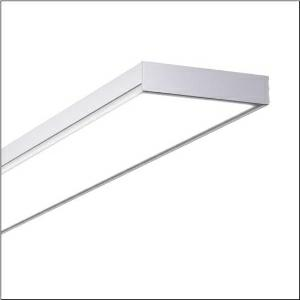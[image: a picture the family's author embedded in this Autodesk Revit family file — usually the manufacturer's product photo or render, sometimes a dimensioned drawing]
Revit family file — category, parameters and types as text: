
# Revit family: apollon_r__31_51mp25wm2441e_54ac
name_source: partatom
category: Lighting Fixtures
units: mm (PartAtom-declared; Revit-internal decimal feet)

## family parameters
Cut with Voids When Loaded = No
Host = Face
Light Source = No
Part Type = Normal
Room Calculation Point = No
Round Connector Dimension = Use Diameter
Shared = No

## types (1)
- Apollon® 31 (1 x LED, 3800 lm, 27 W, 4000K)
    Apparent Load = 27 VA
    CIE Flux Codes = 61 87 97 97 100
    Color Rendering = 80
    Color Temperature = 4000K
    Default Elevation = 1800 mm
    Description = Apollon® 31, office luminaire, primary optical cover: micro prismatic cover, of PMMA, light emission: direct distribution, primary light characteristic: symmetric, installation type: surface-mounted, LED, rated luminous flux: 3.800lm, luminous efficacy: 139lm/W, light colour: 840, colour temperature: 4000K, control gear: ECG Multilumen, with terminal, 3-pole, mains connection: 220..240V, AC, 50/60Hz, rated input power: 27W, housing, of sheet steel, coil coated, metallic grey (RAL 9006), length: 1.245mm, width: 200mm, height: 44mm, protection rating (complete): IP20, insulation class (complete): insulation class II (safety insulation), certification: CE, impact resistance: IK02, permissible operating ambient temperature: -20..+40°C, packaging unit: 1 piece
    Height = 44 mm
    Lamp = 1 x LED
    Lamp Light Flux = 3800 lm
    Lamp Power = 27 W
    Lamp count = 1
    Length = 1245 mm
    Luminous efficacy = 141 lm/W
    Manufacturer = Siteco
    ModVariant = No
    Model = 51MP25WM2441E
    Mounting Place = Ceiling
    Mounting Type = Surface mounted
    Number of Poles = 1
    OnlyDefault = Yes
    Power Factor = 1
    Product Name = Apollon® 31
    Product group = office luminaire | ceiling mounted
    ProductGroupID = 302
    Protection Class = Protection class II
    Protection Degree = IP 20
    RLX_Detail_Level = 1
    RlxData = <blob elided: 24085 chars, md5=8047bcf0>
    Socket = socket
    Standby Power = 0 W
    System Light Flux = 3800 lm
    System Power = 27 W
    Type Comments = Product without accessories
    Type Image = l_1007091.jpg
    URL = http://relux.com
    VarID = ---
    Voltage = 0 V
    Weight = 0.00 kg
    Width = 200 mm  [stored 0.656168 ft]

note: [stored X ft] marks values corroborated as IEEE doubles in the binary element streams (Revit-internal decimal feet)

## geometry (parser evidence)
native form markers: Blend x4, Sweep x9
no freeform markers — native parametric forms only
